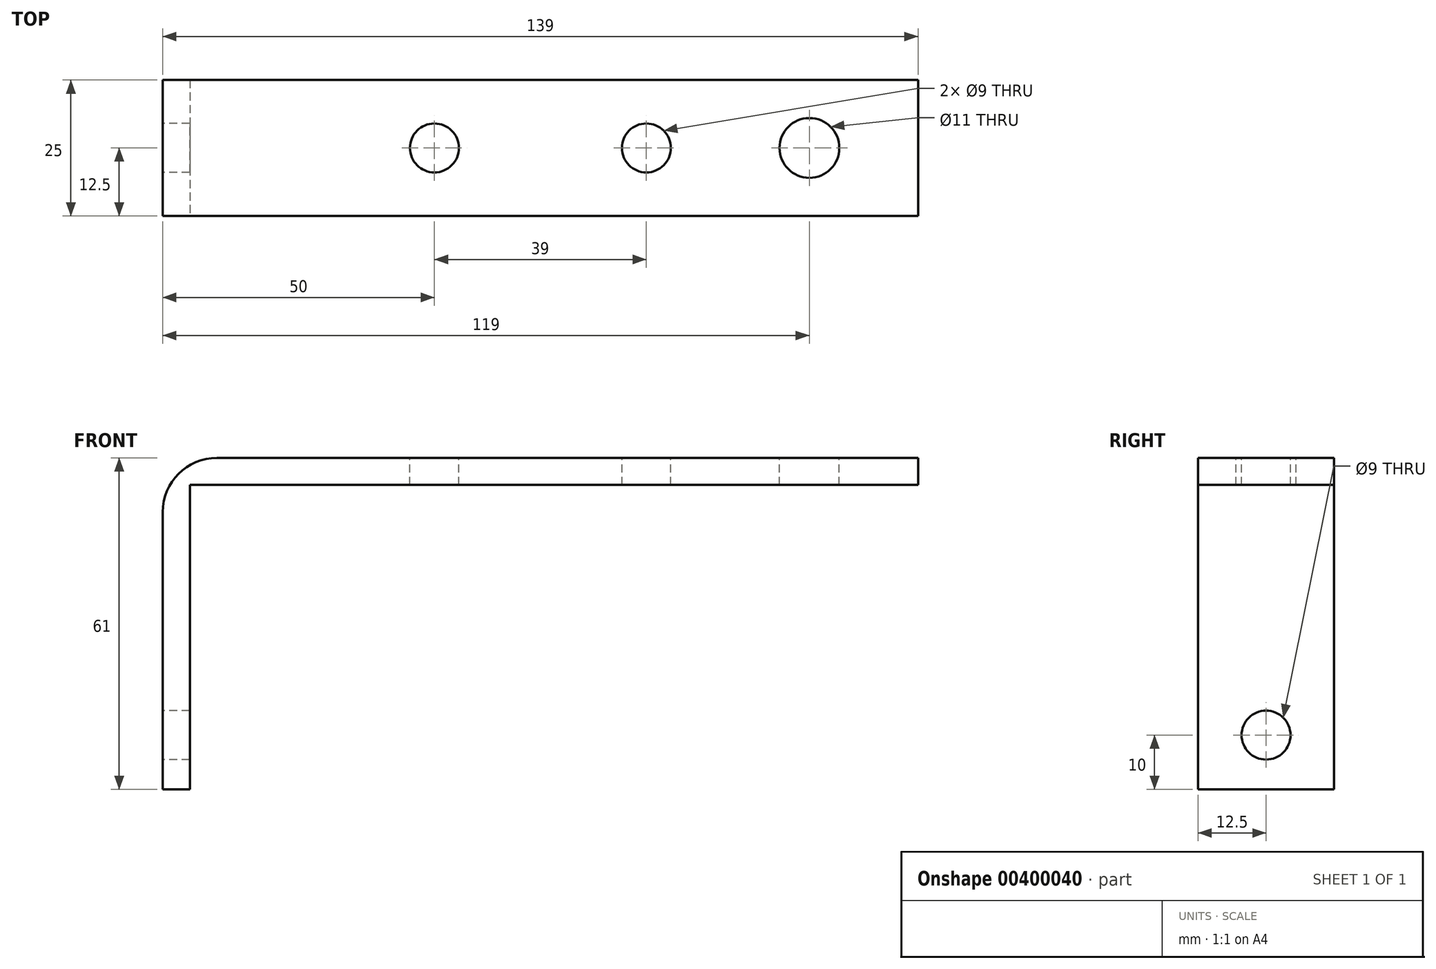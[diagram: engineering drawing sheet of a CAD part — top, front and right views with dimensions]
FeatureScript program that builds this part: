
annotation { "Feature Type Name" : "Feature", "Feature Type Description" : "" }
export const myFeature = defineFeature(function(context is Context, id is Id, definition is map)
    precondition{}
    {
        {
            var Q0;
            Q0=qCreatedBy(makeId("Front.planeOp"),FACE);
            var sketch = newSketch(context, id + "F0", { "sketchPlane" : qUnion([Q0])});
            skLineSegment(sketch, "E0.bottom", {"start": v(134, 5) * mm, "end": v(0, 5) * mm});
            skLineSegment(sketch, "E0.top", {"start": v(134, 0) * mm, "end": v(0, 0) * mm});
            skLineSegment(sketch, "E0.left", {"start": v(134, 5) * mm, "end": v(134, 0) * mm});
            skLineSegment(sketch, "E0.right", {"start": v(0, 5) * mm, "end": v(0, 0) * mm});
            skLineSegment(sketch, "E1.bottom", {"start": v(0, 5) * mm, "end": v(-5, 5) * mm});
            skLineSegment(sketch, "E1.top", {"start": v(0, -56) * mm, "end": v(-5, -56) * mm});
            skLineSegment(sketch, "E1.left", {"start": v(0, 5) * mm, "end": v(0, -56) * mm});
            skLineSegment(sketch, "E1.right", {"start": v(-5, 5) * mm, "end": v(-5, -56) * mm});
            skLineSegment(sketch, "E2", {"start": v(0, 0) * mm, "end": v(5, 0) * mm});
            skArc(sketch, "E3", {"start": v(5, 0) * mm, "mid": v(1.46, -1.46) * mm, "end": v(0, -5) * mm});
            skArc(sketch, "E4.0", {"start": v(5, 5) * mm, "mid": v(-2.07, 2.07) * mm, "end": v(-5, -5) * mm});
            skSolve(sketch);
        }
        {
            var Q0;
            Q0=makeQuery(id+"F0.imprint","IMPRINT",FACE,{"disambiguationData":[TD([[makeQuery(id+"F0.imprint","IMPRINT",EDGE,{"derivedFrom":sQuery(id+"F0.wireOp",EDGE,"E0.top")}),-1.0]])]});
            var Q1;
            {var subQ1=sQuery(id+"F0.wireOp",EDGE,"E1.top");Q1=makeQuery(id+"F0.imprint","IMPRINT",FACE,{"disambiguationData":[TD([[makeQuery(id+"F0.imprint","IMPRINT",EDGE,{"derivedFrom":subQ1}),-1.0]])]});}
            var Q2;
            {var subQ0=sQuery(id+"F0.wireOp",EDGE,"E2");Q2=makeQuery(id+"F0.imprint","IMPRINT",FACE,{"disambiguationData":[TD([[makeQuery(id+"F0.imprint","IMPRINT",EDGE,{"derivedFrom":subQ0}),-1.0]])]});}
            extrude(context, id + "F1", {"entities" : qUnion([Q0, Q1, Q2]), "oppositeDirection" : true, "depth" : 25 * mm});
        }
        {
            var Q0;
            Q0=makeQuery(id+"F1.opExtrude","SWEPT_FACE",FACE,{"disambiguationData":[OSD([sQuery(id+"F0.wireOp",EDGE,"E0.bottom")])]});
            var sketch = newSketch(context, id + "F2", { "sketchPlane" : qUnion([Q0])});
            skCircle(sketch, "E5", {"center": v(114, 12.5) * mm, "radius": 5.5 * mm});
            skCircle(sketch, "E6", {"center": v(84, 12.5) * mm, "radius": 4.5 * mm});
            skCircle(sketch, "E7", {"center": v(45, 12.5) * mm, "radius": 4.5 * mm});
            skSolve(sketch);
        }
        {
            var Q0;
            Q0=qSketchRegion(id+"F2",true);
            extrude(context, id + "F3", {"entities" : qUnion([Q0]), "operationType" : NewBodyOperationType.REMOVE, "oppositeDirection" : true, "depth" : 5 * mm});
        }
        {
            var Q0;
            Q0=qSketchRegion(id+"F2",true);
            extrude(context, id + "F4", {"entities" : qUnion([Q0]), "operationType" : NewBodyOperationType.REMOVE, "oppositeDirection" : true, "depth" : 5 * mm});
        }
        {
            var Q0;
            Q0=makeQuery(id+"F1.opExtrude","SWEPT_FACE",FACE,{"disambiguationData":[OSD([sQuery(id+"F0.wireOp",EDGE,"E1.right")])]});
            var sketch = newSketch(context, id + "F5", { "sketchPlane" : qUnion([Q0])});
            skLineSegment(sketch, "E8", {"start": v(-12.5, -56) * mm, "end": v(-12.5, -46) * mm});
            skCircle(sketch, "E9", {"center": v(-12.5, -46) * mm, "radius": 4.5 * mm});
            skSolve(sketch);
        }
        {
            var Q0;
            Q0=qSketchRegion(id+"F5",true);
            extrude(context, id + "F6", {"entities" : qUnion([Q0]), "operationType" : NewBodyOperationType.REMOVE, "oppositeDirection" : true, "depth" : 5 * mm});
        }
    });
